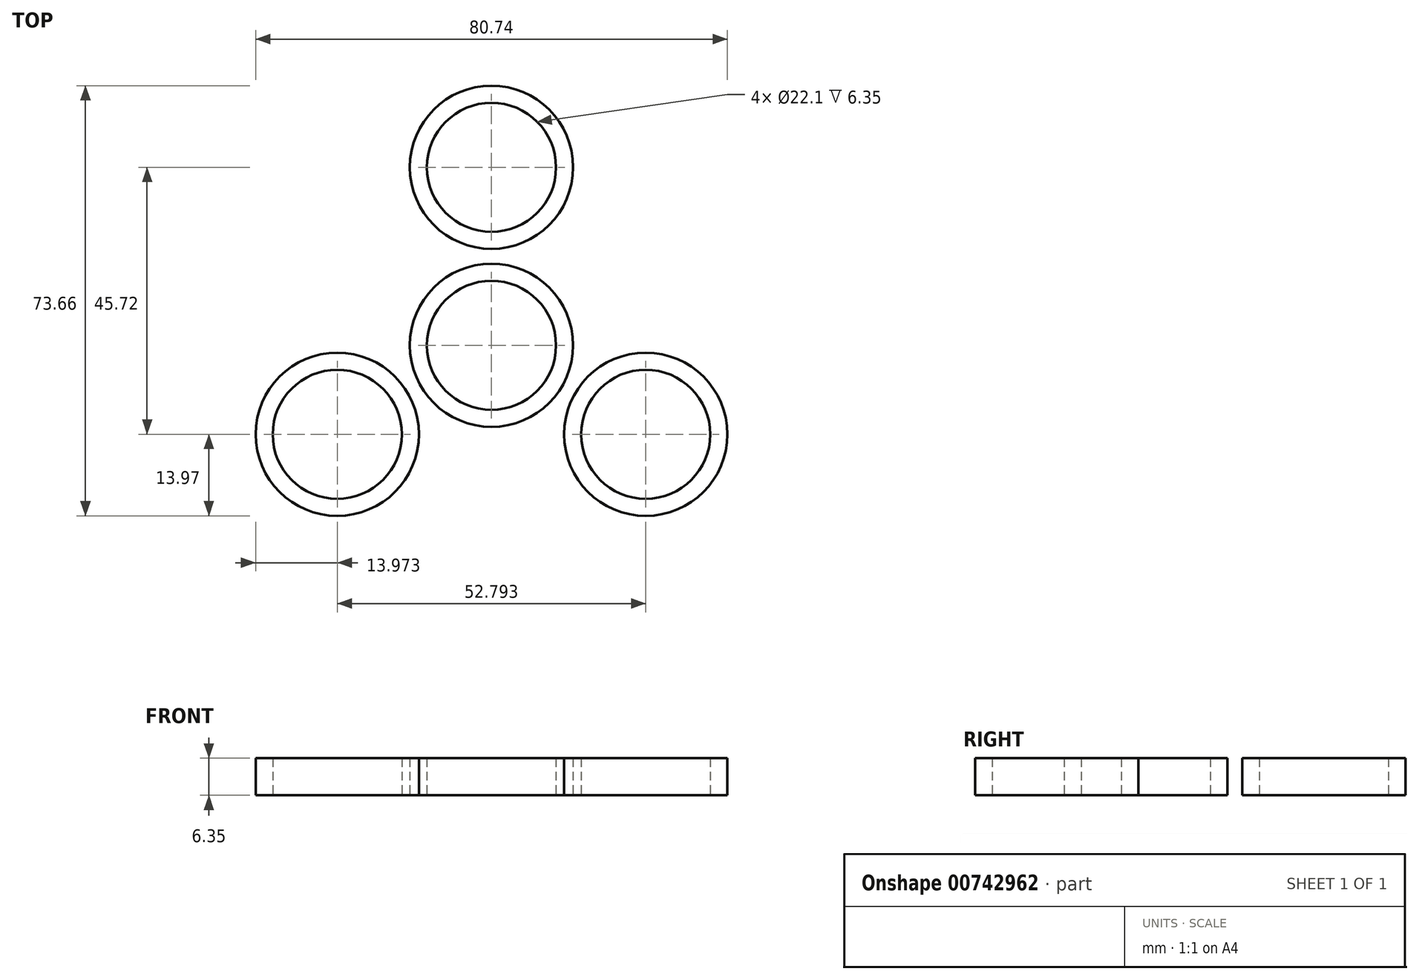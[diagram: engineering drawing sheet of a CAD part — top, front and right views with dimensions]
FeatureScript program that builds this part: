
annotation { "Feature Type Name" : "Feature", "Feature Type Description" : "" }
export const myFeature = defineFeature(function(context is Context, id is Id, definition is map)
    precondition{}
    {
        {
            var Q0;
            Q0=qCreatedBy(makeId("Top.planeOp"),FACE);
            var sketch = newSketch(context, id + "F0", { "sketchPlane" : qUnion([Q0])});
            skCircle(sketch, "E0", {"center": v(0, 0) * mm, "radius": 11.05 * mm});
            skCircle(sketch, "E1", {"center": v(0, 0) * mm, "radius": 13.97 * mm});
            skLineSegment(sketch, "E2", {"start": v(0, 0) * mm, "end": v(0, 30.48) * mm});
            skCircle(sketch, "E3", {"center": v(0, 30.48) * mm, "radius": 11.05 * mm});
            skLineSegment(sketch, "E4", {"start": v(14.11, 13.5) * mm, "end": v(14.15, 17.72) * mm});
            skLineSegment(sketch, "E5", {"start": v(15.46, 46.9) * mm, "end": v(16.13, 49.58) * mm});
            skLineSegment(sketch, "E6", {"start": v(19.24, 53.62) * mm, "end": v(19.81, 53.93) * mm});
            skPoint(sketch, "E7.visualSharp", {"position": v(16.8, 52.28) * mm});
            skArc(sketch, "E7.filletArc", {"start": v(19.24, 53.62) * mm, "mid": v(17.26, 51.92) * mm, "end": v(16.13, 49.58) * mm});
            skPoint(sketch, "E8.visualSharp", {"position": v(14.17, 41.71) * mm});
            skArc(sketch, "E8.filletArc", {"start": v(15.46, 46.9) * mm, "mid": v(15.3, 44.89) * mm, "end": v(15.76, 42.93) * mm});
            skPoint(sketch, "E9.visualSharp", {"position": v(21.55, 30.24) * mm});
            skPoint(sketch, "E10.visualSharp", {"position": v(14.17, 19.69) * mm});
            skArc(sketch, "E10.filletArc", {"start": v(15.3, 21.3) * mm, "mid": v(14.46, 19.6) * mm, "end": v(14.15, 17.72) * mm});
            skCircle(sketch, "E11", {"center": v(0, 30.48) * mm, "radius": 13.97 * mm});
            skLineSegment(sketch, "E12", {"start": v(22.44, 56.66) * mm, "end": v(23.64, 59.06) * mm});
            skLineSegment(sketch, "E13", {"start": v(16.01, 54.88) * mm, "end": v(14.76, 54.2) * mm});
            skLineSegment(sketch, "E14", {"start": v(11.46, 48.63) * mm, "end": v(11.46, 47.72) * mm});
            skPoint(sketch, "E15.visualSharp", {"position": v(11.46, 52.39) * mm});
            skArc(sketch, "E15.filletArc", {"start": v(14.76, 54.2) * mm, "mid": v(12.35, 51.86) * mm, "end": v(11.46, 48.63) * mm});
            skLineSegment(sketch, "E16", {"start": v(11.46, 57.17) * mm, "end": v(11.72, 57.53) * mm});
            skLineSegment(sketch, "E17", {"start": v(11.36, 65.5) * mm, "end": v(11.2, 65.69) * mm});
            skLineSegment(sketch, "E18", {"start": v(9.63, 69.34) * mm, "end": v(9.22, 74.02) * mm});
            skPoint(sketch, "E19.visualSharp", {"position": v(9.8, 67.26) * mm});
            skArc(sketch, "E19.filletArc", {"start": v(9.63, 69.34) * mm, "mid": v(10.12, 67.39) * mm, "end": v(11.2, 65.69) * mm});
            skPoint(sketch, "E20.visualSharp", {"position": v(14.76, 61.66) * mm});
            skLineSegment(sketch, "E21", {"start": v(9.22, 74.02) * mm, "end": v(6.36, 67.59) * mm});
            skLineSegment(sketch, "E22", {"start": v(6.05, 63.3) * mm, "end": v(6.37, 62.13) * mm});
            skPoint(sketch, "E23.visualSharp", {"position": v(5.43, 65.5) * mm});
            skArc(sketch, "E23.filletArc", {"start": v(6.36, 67.59) * mm, "mid": v(5.83, 65.47) * mm, "end": v(6.05, 63.3) * mm});
            skLineSegment(sketch, "E24", {"start": v(4.05, 52.67) * mm, "end": v(2.95, 51.63) * mm});
            skPoint(sketch, "E25.visualSharp", {"position": v(6.6, 55.05) * mm});
            skLineSegment(sketch, "E26", {"start": v(2.95, 51.63) * mm, "end": v(2.95, 59.37) * mm});
            skLineSegment(sketch, "E27", {"start": v(1.24, 63.7) * mm, "end": v(-5.43, 70.86) * mm});
            skLineSegment(sketch, "E28", {"start": v(-5.43, 70.86) * mm, "end": v(-9.03, 79.2) * mm});
            skLineSegment(sketch, "E29", {"start": v(-9.03, 79.2) * mm, "end": v(-11.48, 70) * mm});
            skPoint(sketch, "E30.visualSharp", {"position": v(-12.25, 67.14) * mm});
            skArc(sketch, "E30.filletArc", {"start": v(-11.48, 70) * mm, "mid": v(-11.6, 67.26) * mm, "end": v(-10.55, 64.72) * mm});
            skLineSegment(sketch, "E31", {"start": v(-10.55, 64.72) * mm, "end": v(-8.8, 62.23) * mm});
            skLineSegment(sketch, "E32", {"start": v(-7.97, 56.58) * mm, "end": v(-10.55, 48.84) * mm});
            skPoint(sketch, "E33.visualSharp", {"position": v(-6.96, 59.62) * mm});
            skArc(sketch, "E33.filletArc", {"start": v(-7.97, 56.58) * mm, "mid": v(-7.72, 59.5) * mm, "end": v(-8.8, 62.23) * mm});
            skPoint(sketch, "E34.visualSharp", {"position": v(2.95, 61.87) * mm});
            skArc(sketch, "E34.filletArc", {"start": v(2.95, 59.37) * mm, "mid": v(2.5, 61.7) * mm, "end": v(1.24, 63.7) * mm});
            skLineSegment(sketch, "E35", {"start": v(11.2, 65.69) * mm, "end": v(12.45, 63.76) * mm});
            skLineSegment(sketch, "E36", {"start": v(13.46, 60.3) * mm, "end": v(13.46, 59.67) * mm});
            skLineSegment(sketch, "E37", {"start": v(13.18, 57.78) * mm, "end": v(12.3, 54.98) * mm});
            skLineSegment(sketch, "E38", {"start": v(12.3, 54.98) * mm, "end": v(11.46, 48.63) * mm});
            skPoint(sketch, "E39.visualSharp", {"position": v(13.46, 62.18) * mm});
            skArc(sketch, "E39.filletArc", {"start": v(13.46, 60.3) * mm, "mid": v(13.2, 62.1) * mm, "end": v(12.45, 63.76) * mm});
            skPoint(sketch, "E40.visualSharp", {"position": v(13.46, 58.7) * mm});
            skArc(sketch, "E40.filletArc", {"start": v(13.18, 57.78) * mm, "mid": v(13.4, 58.72) * mm, "end": v(13.46, 59.67) * mm});
            skLineSegment(sketch, "E41", {"start": v(6.6, 60.41) * mm, "end": v(6.6, 58.64) * mm});
            skLineSegment(sketch, "E42", {"start": v(6.38, 56.96) * mm, "end": v(6.13, 56.04) * mm});
            skLineSegment(sketch, "E43", {"start": v(5.28, 54.19) * mm, "end": v(5, 53.77) * mm});
            skPoint(sketch, "E44.visualSharp", {"position": v(6.6, 61.29) * mm});
            skArc(sketch, "E44.filletArc", {"start": v(6.6, 60.41) * mm, "mid": v(6.55, 61.28) * mm, "end": v(6.37, 62.13) * mm});
            skPoint(sketch, "E45.visualSharp", {"position": v(6.6, 57.78) * mm});
            skArc(sketch, "E45.filletArc", {"start": v(6.38, 56.96) * mm, "mid": v(6.55, 57.8) * mm, "end": v(6.6, 58.64) * mm});
            skPoint(sketch, "E46.visualSharp", {"position": v(5.85, 55.05) * mm});
            skArc(sketch, "E46.filletArc", {"start": v(5.28, 54.19) * mm, "mid": v(5.78, 55.08) * mm, "end": v(6.13, 56.04) * mm});
            skPoint(sketch, "E47.visualSharp", {"position": v(4.59, 53.16) * mm});
            skArc(sketch, "E47.filletArc", {"start": v(4.05, 52.67) * mm, "mid": v(4.55, 53.19) * mm, "end": v(5, 53.77) * mm});
            skPoint(sketch, "E48.visualSharp", {"position": v(21.55, 54.88) * mm});
            skArc(sketch, "E48.filletArc", {"start": v(19.81, 53.93) * mm, "mid": v(21.33, 55.1) * mm, "end": v(22.44, 56.66) * mm});
            skLineSegment(sketch, "E49", {"start": v(16.01, 54.88) * mm, "end": v(19.12, 56.04) * mm});
            skLineSegment(sketch, "E50", {"start": v(19.12, 56.04) * mm, "end": v(19.79, 56.27) * mm});
            skLineSegment(sketch, "E51", {"start": v(21.97, 57.56) * mm, "end": v(23.64, 59.06) * mm});
            skPoint(sketch, "E52.visualSharp", {"position": v(21, 56.7) * mm});
            skArc(sketch, "E52.filletArc", {"start": v(19.79, 56.27) * mm, "mid": v(20.94, 56.8) * mm, "end": v(21.97, 57.56) * mm});
            skCircle(sketch, "E53.1.0", {"center": v(-26.4, -15.24) * mm, "radius": 11.05 * mm});
            skCircle(sketch, "E53.2.0", {"center": v(26.4, -15.24) * mm, "radius": 11.05 * mm});
            skCircle(sketch, "E54.1.0", {"center": v(-26.4, -15.24) * mm, "radius": 13.97 * mm});
            skCircle(sketch, "E54.2.0", {"center": v(26.4, -15.24) * mm, "radius": 13.97 * mm});
            skLineSegment(sketch, "E55", {"start": v(15.76, 42.93) * mm, "end": v(17.73, 35.28) * mm});
            skLineSegment(sketch, "E56", {"start": v(17.53, 28.22) * mm, "end": v(15.3, 21.3) * mm});
            skPoint(sketch, "E57.visualSharp", {"position": v(18.65, 31.72) * mm});
            skArc(sketch, "E57.filletArc", {"start": v(17.53, 28.22) * mm, "mid": v(18.13, 31.74) * mm, "end": v(17.73, 35.28) * mm});
            skSolve(sketch);
        }
        {
            var Q0;
            Q0=makeQuery(id+"F0.imprint","IMPRINT",FACE,{"disambiguationData":[TD([[makeQuery(id+"F0.imprint","IMPRINT",EDGE,{"derivedFrom":sQuery(id+"F0.wireOp",EDGE,"E4")}),1.0]])]});
            var Q1;
            Q1=makeQuery(id+"F0.imprint","IMPRINT",FACE,{"disambiguationData":[TD([[makeQuery(id+"F0.imprint","IMPRINT",EDGE,{"derivedFrom":sQuery(id+"F0.wireOp",EDGE,"E3")}),-1.0]])]});
            var Q2;
            Q2=makeQuery(id+"F0.imprint","IMPRINT",FACE,{"disambiguationData":[TD([[makeQuery(id+"F0.imprint","IMPRINT",EDGE,{"derivedFrom":sQuery(id+"F0.wireOp",EDGE,"E53.2.0")}),-1.0]])]});
            var Q3;
            Q3=makeQuery(id+"F0.imprint","IMPRINT",FACE,{"disambiguationData":[TD([[makeQuery(id+"F0.imprint","IMPRINT",EDGE,{"derivedFrom":sQuery(id+"F0.wireOp",EDGE,"E53.1.0")}),-1.0]])]});
            var Q4;
            Q4=makeQuery(id+"F0.imprint","IMPRINT",FACE,{"disambiguationData":[TD([[makeQuery(id+"F0.imprint","IMPRINT",EDGE,{"derivedFrom":sQuery(id+"F0.wireOp",EDGE,"E0")}),-1.0]])]});
            extrude(context, id + "F1", {"entities" : qUnion([Q0, Q1, Q2, Q3, Q4]), "depth" : 6.35 * mm, "offsetDistance" : 25.4 * mm});
        }
    });
